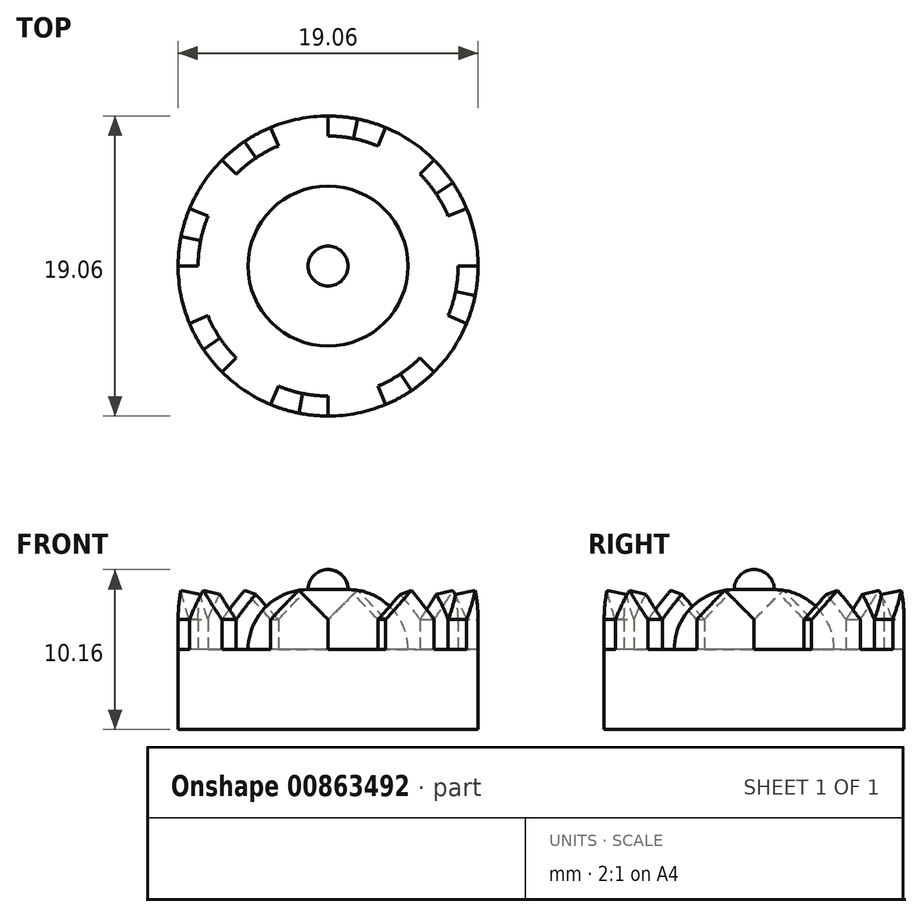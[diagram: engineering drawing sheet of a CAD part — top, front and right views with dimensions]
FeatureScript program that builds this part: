
annotation { "Feature Type Name" : "Feature", "Feature Type Description" : "" }
export const myFeature = defineFeature(function(context is Context, id is Id, definition is map)
    precondition{}
    {
        {
            var Q0;
            Q0=qCreatedBy(makeId("Top.planeOp"),FACE);
            var sketch = newSketch(context, id + "F0", { "sketchPlane" : qUnion([Q0])});
            skCircle(sketch, "E0", {"center": v(0, 0) * mm, "radius": 9.53 * mm});
            skLineSegment(sketch, "E1", {"start": v(0, 9.53) * mm, "end": v(0, 8.26) * mm});
            skLineSegment(sketch, "E2", {"start": v(3.16, 7.63) * mm, "end": v(3.65, 8.8) * mm});
            skLineSegment(sketch, "E3", {"start": v(5.84, 5.84) * mm, "end": v(6.74, 6.74) * mm});
            skLineSegment(sketch, "E4", {"start": v(8.26, 0) * mm, "end": v(9.77, 0) * mm});
            skLineSegment(sketch, "E5", {"start": v(7.63, 3.16) * mm, "end": v(8.8, 3.65) * mm});
            skArc(sketch, "E6", {"start": v(3.16, 7.63) * mm, "mid": v(1.61, 8.1) * mm, "end": v(0, 8.26) * mm});
            skArc(sketch, "E7.trimOffspring", {"start": v(7.63, 3.16) * mm, "mid": v(6.86, 4.59) * mm, "end": v(5.84, 5.84) * mm});
            skLineSegment(sketch, "E8", {"start": v(5.84, -5.84) * mm, "end": v(6.74, -6.74) * mm});
            skLineSegment(sketch, "E9", {"start": v(7.63, -3.16) * mm, "end": v(8.8, -3.65) * mm});
            skLineSegment(sketch, "E10", {"start": v(3.16, -7.63) * mm, "end": v(3.65, -8.8) * mm});
            skArc(sketch, "E11.trimOffspring", {"start": v(7.63, -3.16) * mm, "mid": v(8.1, -1.61) * mm, "end": v(8.26, 0) * mm});
            skArc(sketch, "E12.trimOffspring", {"start": v(3.16, -7.63) * mm, "mid": v(4.59, -6.86) * mm, "end": v(5.84, -5.84) * mm});
            skLineSegment(sketch, "E13", {"start": v(-8.26, 0) * mm, "end": v(-9.53, 0) * mm});
            skLineSegment(sketch, "E14", {"start": v(-5.84, 5.84) * mm, "end": v(-6.74, 6.74) * mm});
            skLineSegment(sketch, "E15", {"start": v(-7.63, 3.16) * mm, "end": v(-8.8, 3.65) * mm});
            skLineSegment(sketch, "E16", {"start": v(-3.16, 7.63) * mm, "end": v(-3.65, 8.8) * mm});
            skLineSegment(sketch, "E17", {"start": v(-7.63, -3.16) * mm, "end": v(-8.8, -3.65) * mm});
            skLineSegment(sketch, "E18", {"start": v(-5.84, -5.84) * mm, "end": v(-6.74, -6.74) * mm});
            skLineSegment(sketch, "E19", {"start": v(-3.16, -7.63) * mm, "end": v(-3.65, -8.8) * mm});
            skArc(sketch, "E20.trimOffspring", {"start": v(-3.16, -7.63) * mm, "mid": v(-1.61, -8.1) * mm, "end": v(0, -8.26) * mm});
            skArc(sketch, "E21.trimOffspring", {"start": v(-7.63, -3.16) * mm, "mid": v(-6.86, -4.59) * mm, "end": v(-5.84, -5.84) * mm});
            skArc(sketch, "E22.trimOffspring", {"start": v(-7.63, 3.16) * mm, "mid": v(-8.1, 1.61) * mm, "end": v(-8.26, 0) * mm});
            skArc(sketch, "E23.trimOffspring", {"start": v(-3.16, 7.63) * mm, "mid": v(-4.59, 6.86) * mm, "end": v(-5.84, 5.84) * mm});
            skLineSegment(sketch, "E24.trimOffspring", {"start": v(0, -8.26) * mm, "end": v(0, -9.53) * mm});
            skSolve(sketch);
        }
        {
            var Q0;
            {var subQ1=sQuery(id+"F0.wireOp",EDGE,"E1");var subQ3=sQuery(id+"F0.wireOp",EDGE,"E6");var subQ4=makeQuery(id+"F0.imprint","INTERSECT",VERTEX,{"disambiguationData":[OD(0.0)],"derivedFrom":[subQ1,subQ3]});Q0=makeQuery(id+"F0.imprint","IMPRINT",FACE,{"disambiguationData":[TD([[makeQuery(id+"F0.imprint","IMPRINT",EDGE,{"disambiguationData":[TD([[subQ4,1.0]])],"derivedFrom":subQ3}),1.0]])]});}
            var Q1;
            {var subQ0=sQuery(id+"F0.wireOp",EDGE,"E1");var subQ2=sQuery(id+"F0.wireOp",EDGE,"E6");var subQ3=makeQuery(id+"F0.imprint","INTERSECT",VERTEX,{"disambiguationData":[OD(0.0)],"derivedFrom":[subQ0,subQ2]});Q1=makeQuery(id+"F0.imprint","IMPRINT",FACE,{"disambiguationData":[TD([[makeQuery(id+"F0.imprint","IMPRINT",EDGE,{"disambiguationData":[TD([[subQ3,-1.0]])],"derivedFrom":subQ2}),1.0]])]});}
            var Q2;
            {var subQ1=sQuery(id+"F0.wireOp",EDGE,"E1");var subQ3=sQuery(id+"F0.wireOp",EDGE,"E6");var subQ4=makeQuery(id+"F0.imprint","INTERSECT",VERTEX,{"disambiguationData":[OD(1.0)],"derivedFrom":[subQ1,subQ3]});Q2=makeQuery(id+"F0.imprint","IMPRINT",FACE,{"disambiguationData":[TD([[makeQuery(id+"F0.imprint","IMPRINT",EDGE,{"disambiguationData":[TD([[subQ4,-1.0]])],"derivedFrom":subQ3}),1.0]])]});}
            var Q3;
            {var subQ1=sQuery(id+"F0.wireOp",EDGE,"E4");var subQ3=sQuery(id+"F0.wireOp",EDGE,"E6");var subQ4=makeQuery(id+"F0.imprint","INTERSECT",VERTEX,{"derivedFrom":[subQ1,subQ3]});Q3=makeQuery(id+"F0.imprint","IMPRINT",FACE,{"disambiguationData":[TD([[makeQuery(id+"F0.imprint","IMPRINT",EDGE,{"disambiguationData":[TD([[subQ4,-1.0]])],"derivedFrom":subQ3}),1.0]])]});}
            var Q4;
            {var subQ1=sQuery(id+"F0.wireOp",EDGE,"E3");var subQ3=sQuery(id+"F0.wireOp",EDGE,"E6");var subQ4=makeQuery(id+"F0.imprint","INTERSECT",VERTEX,{"derivedFrom":[subQ1,subQ3]});Q4=makeQuery(id+"F0.imprint","IMPRINT",FACE,{"disambiguationData":[TD([[makeQuery(id+"F0.imprint","IMPRINT",EDGE,{"disambiguationData":[TD([[subQ4,1.0]])],"derivedFrom":subQ3}),1.0]])]});}
            var Q5;
            {var subQ1=sQuery(id+"F0.wireOp",EDGE,"E2");var subQ3=sQuery(id+"F0.wireOp",EDGE,"E6");var subQ4=makeQuery(id+"F0.imprint","INTERSECT",VERTEX,{"derivedFrom":[subQ1,subQ3]});Q5=makeQuery(id+"F0.imprint","IMPRINT",FACE,{"disambiguationData":[TD([[makeQuery(id+"F0.imprint","IMPRINT",EDGE,{"disambiguationData":[TD([[subQ4,1.0]])],"derivedFrom":subQ3}),1.0]])]});}
            var Q6;
            {var subQ0=sQuery(id+"F0.wireOp",EDGE,"E2");var subQ1=sQuery(id+"F0.wireOp",EDGE,"E0");var subQ2=makeQuery(id+"F0.imprint","INTERSECT",VERTEX,{"derivedFrom":[subQ1,subQ0]});Q6=makeQuery(id+"F0.imprint","IMPRINT",FACE,{"disambiguationData":[TD([[makeQuery(id+"F0.imprint","IMPRINT",EDGE,{"disambiguationData":[TD([[subQ2,1.0]])],"derivedFrom":subQ1}),1.0]])]});}
            var Q7;
            {var subQ0=sQuery(id+"F0.wireOp",EDGE,"E5");var subQ1=sQuery(id+"F0.wireOp",EDGE,"E0");var subQ2=makeQuery(id+"F0.imprint","INTERSECT",VERTEX,{"derivedFrom":[subQ1,subQ0]});Q7=makeQuery(id+"F0.imprint","IMPRINT",FACE,{"disambiguationData":[TD([[makeQuery(id+"F0.imprint","IMPRINT",EDGE,{"disambiguationData":[TD([[subQ2,1.0]])],"derivedFrom":subQ1}),1.0]])]});}
            var Q8;
            {var subQ8=sQuery(id+"F0.wireOp",EDGE,"E8");Q8=makeQuery(id+"F0.imprint","IMPRINT",FACE,{"disambiguationData":[TD([[makeQuery(id+"F0.imprint","IMPRINT",EDGE,{"derivedFrom":subQ8}),1.0]])]});}
            extrude(context, id + "F1", {"entities" : qUnion([Q0, Q1, Q2, Q3, Q4, Q5, Q6, Q7, Q8]), "depth" : 5.08 * mm, "offsetDistance" : 25.4 * mm});
        }
        {
            var Q0;
            {var subQ0=sQuery(id+"F0.wireOp",EDGE,"E1");var subQ1=sQuery(id+"F0.wireOp",EDGE,"E0");var subQ2=makeQuery(id+"F0.imprint","INTERSECT",VERTEX,{"disambiguationData":[OD(0.0)],"derivedFrom":[subQ1,subQ0]});Q0=makeQuery(id+"F0.imprint","IMPRINT",FACE,{"disambiguationData":[TD([[makeQuery(id+"F0.imprint","IMPRINT",EDGE,{"disambiguationData":[TD([[subQ2,1.0]])],"derivedFrom":subQ1}),1.0]])]});}
            var Q1;
            {var subQ0=sQuery(id+"F0.wireOp",EDGE,"E3");var subQ1=sQuery(id+"F0.wireOp",EDGE,"E0");var subQ2=makeQuery(id+"F0.imprint","INTERSECT",VERTEX,{"derivedFrom":[subQ1,subQ0]});Q1=makeQuery(id+"F0.imprint","IMPRINT",FACE,{"disambiguationData":[TD([[makeQuery(id+"F0.imprint","IMPRINT",EDGE,{"disambiguationData":[TD([[subQ2,1.0]])],"derivedFrom":subQ1}),1.0]])]});}
            var Q2;
            {var subQ0=sQuery(id+"F0.wireOp",EDGE,"E8");Q2=makeQuery(id+"F0.imprint","IMPRINT",FACE,{"disambiguationData":[TD([[makeQuery(id+"F0.imprint","IMPRINT",EDGE,{"derivedFrom":subQ0}),-1.0]])]});}
            var Q3;
            {var subQ0=sQuery(id+"F0.wireOp",EDGE,"E9");Q3=makeQuery(id+"F0.imprint","IMPRINT",FACE,{"disambiguationData":[TD([[makeQuery(id+"F0.imprint","IMPRINT",EDGE,{"derivedFrom":subQ0}),1.0]])]});}
            var Q4;
            {var subQ0=sQuery(id+"F0.wireOp",EDGE,"E19");Q4=makeQuery(id+"F0.imprint","IMPRINT",FACE,{"disambiguationData":[TD([[makeQuery(id+"F0.imprint","IMPRINT",EDGE,{"derivedFrom":subQ0}),1.0]])]});}
            var Q5;
            {var subQ0=sQuery(id+"F0.wireOp",EDGE,"E17");Q5=makeQuery(id+"F0.imprint","IMPRINT",FACE,{"disambiguationData":[TD([[makeQuery(id+"F0.imprint","IMPRINT",EDGE,{"derivedFrom":subQ0}),1.0]])]});}
            var Q6;
            {var subQ0=sQuery(id+"F0.wireOp",EDGE,"E13");Q6=makeQuery(id+"F0.imprint","IMPRINT",FACE,{"disambiguationData":[TD([[makeQuery(id+"F0.imprint","IMPRINT",EDGE,{"derivedFrom":subQ0}),-1.0]])]});}
            var Q7;
            {var subQ0=sQuery(id+"F0.wireOp",EDGE,"E14");Q7=makeQuery(id+"F0.imprint","IMPRINT",FACE,{"disambiguationData":[TD([[makeQuery(id+"F0.imprint","IMPRINT",EDGE,{"derivedFrom":subQ0}),-1.0]])]});}
            extrude(context, id + "F2", {"entities" : qUnion([Q0, Q1, Q2, Q3, Q4, Q5, Q6, Q7]), "operationType" : NewBodyOperationType.ADD, "depth" : 8.9 * mm, "offsetDistance" : 25.4 * mm});
        }
        {
            var Q0;
            Q0=makeQuery(id+"F2.opExtrude","CAP_EDGE",EDGE,{"disambiguationData":[OSD([sQuery(id+"F0.wireOp",EDGE,"E2")])],"isStart":false});
            var Q1;
            Q1=makeQuery(id+"F2.opExtrude","CAP_EDGE",EDGE,{"disambiguationData":[OSD([sQuery(id+"F0.wireOp",EDGE,"E1")])],"isStart":false});
            var Q2;
            Q2=makeQuery(id+"F2.opExtrude","CAP_EDGE",EDGE,{"disambiguationData":[OSD([sQuery(id+"F0.wireOp",EDGE,"E5")])],"isStart":false});
            var Q3;
            Q3=makeQuery(id+"F2.opExtrude","CAP_EDGE",EDGE,{"disambiguationData":[OSD([sQuery(id+"F0.wireOp",EDGE,"E3")])],"isStart":false});
            var Q4;
            Q4=makeQuery(id+"F2.opExtrude","CAP_EDGE",EDGE,{"disambiguationData":[OSD([sQuery(id+"F0.wireOp",EDGE,"E10")])],"isStart":false});
            var Q5;
            Q5=makeQuery(id+"F2.opExtrude","CAP_EDGE",EDGE,{"disambiguationData":[OSD([sQuery(id+"F0.wireOp",EDGE,"E8")])],"isStart":false});
            var Q6;
            Q6=makeQuery(id+"F2.opExtrude","CAP_EDGE",EDGE,{"disambiguationData":[OSD([sQuery(id+"F0.wireOp",EDGE,"E9")])],"isStart":false});
            var Q7;
            Q7=makeQuery(id+"F2.opExtrude","CAP_EDGE",EDGE,{"disambiguationData":[OSD([sQuery(id+"F0.wireOp",EDGE,"E4")])],"isStart":false});
            var Q8;
            Q8=makeQuery(id+"F2.opExtrude","CAP_EDGE",EDGE,{"disambiguationData":[OSD([sQuery(id+"F0.wireOp",EDGE,"E24.trimOffspring")])],"isStart":false});
            var Q9;
            Q9=makeQuery(id+"F2.opExtrude","CAP_EDGE",EDGE,{"disambiguationData":[OSD([sQuery(id+"F0.wireOp",EDGE,"E19")])],"isStart":false});
            var Q10;
            Q10=makeQuery(id+"F2.opExtrude","CAP_EDGE",EDGE,{"disambiguationData":[OSD([sQuery(id+"F0.wireOp",EDGE,"E18")])],"isStart":false});
            var Q11;
            Q11=makeQuery(id+"F2.opExtrude","CAP_EDGE",EDGE,{"disambiguationData":[OSD([sQuery(id+"F0.wireOp",EDGE,"E17")])],"isStart":false});
            var Q12;
            Q12=makeQuery(id+"F2.opExtrude","CAP_EDGE",EDGE,{"disambiguationData":[OSD([sQuery(id+"F0.wireOp",EDGE,"E13")])],"isStart":false});
            var Q13;
            Q13=makeQuery(id+"F2.opExtrude","CAP_EDGE",EDGE,{"disambiguationData":[OSD([sQuery(id+"F0.wireOp",EDGE,"E15")])],"isStart":false});
            var Q14;
            Q14=makeQuery(id+"F2.opExtrude","CAP_EDGE",EDGE,{"disambiguationData":[OSD([sQuery(id+"F0.wireOp",EDGE,"E14")])],"isStart":false});
            var Q15;
            Q15=makeQuery(id+"F2.opExtrude","CAP_EDGE",EDGE,{"disambiguationData":[OSD([sQuery(id+"F0.wireOp",EDGE,"E16")])],"isStart":false});
            chamfer(context, id + "F3", {"entities" : qUnion([Q0, Q1, Q2, Q3, Q4, Q5, Q6, Q7, Q8, Q9, Q10, Q11, Q12, Q13, Q14, Q15]), "width" : 1.9 * mm, "tangentPropagation" : true});
        }
        {
            var Q0;
            Q0=makeQuery(id+"F1.opExtrude","CAP_FACE",FACE,{"disambiguationData":[OSD([sQuery(id+"F0.wireOp",EDGE,"E0"),sQuery(id+"F0.wireOp",EDGE,"E1"),sQuery(id+"F0.wireOp",EDGE,"E2"),sQuery(id+"F0.wireOp",EDGE,"E3"),sQuery(id+"F0.wireOp",EDGE,"E4"),sQuery(id+"F0.wireOp",EDGE,"E5"),sQuery(id+"F0.wireOp",EDGE,"E6"),sQuery(id+"F0.wireOp",EDGE,"E7.trimOffspring"),sQuery(id+"F0.wireOp",EDGE,"E8"),sQuery(id+"F0.wireOp",EDGE,"E9"),sQuery(id+"F0.wireOp",EDGE,"E10"),sQuery(id+"F0.wireOp",EDGE,"E11.trimOffspring"),sQuery(id+"F0.wireOp",EDGE,"E12.trimOffspring"),sQuery(id+"F0.wireOp",EDGE,"E13"),sQuery(id+"F0.wireOp",EDGE,"E14"),sQuery(id+"F0.wireOp",EDGE,"E15"),sQuery(id+"F0.wireOp",EDGE,"E16"),sQuery(id+"F0.wireOp",EDGE,"E17"),sQuery(id+"F0.wireOp",EDGE,"E18"),sQuery(id+"F0.wireOp",EDGE,"E19"),sQuery(id+"F0.wireOp",EDGE,"E20.trimOffspring"),sQuery(id+"F0.wireOp",EDGE,"E21.trimOffspring"),sQuery(id+"F0.wireOp",EDGE,"E22.trimOffspring"),sQuery(id+"F0.wireOp",EDGE,"E23.trimOffspring"),sQuery(id+"F0.wireOp",EDGE,"E24.trimOffspring")])],"isStart":false});
            var sketch = newSketch(context, id + "F4", { "sketchPlane" : qUnion([Q0])});
            skCircle(sketch, "E25", {"center": v(0, 0) * mm, "radius": 5.08 * mm});
            skSolve(sketch);
        }
        {
            var Q0;
            Q0=makeQuery(id+"F4.imprint","IMPRINT",FACE,{"disambiguationData":[TD([[makeQuery(id+"F4.imprint","IMPRINT",EDGE,{"derivedFrom":sQuery(id+"F4.wireOp",EDGE,"E25")}),1.0]])]});
            extrude(context, id + "F5", {"entities" : qUnion([Q0]), "operationType" : NewBodyOperationType.ADD, "depth" : 3.8 * mm, "offsetDistance" : 25.4 * mm});
        }
        {
            var Q0;
            Q0=makeQuery(id+"F5.opExtrude","CAP_EDGE",EDGE,{"disambiguationData":[OSD([sQuery(id+"F4.wireOp",EDGE,"E25")])],"isStart":false});
            fillet(context, id + "F6", {"entities" : qUnion([Q0]), "radius" : 3.8 * mm, "tangentPropagation" : true, "allowEdgeOverflow" : false});
        }
        {
            var Q0;
            Q0=makeQuery(id+"F5.opExtrude","CAP_FACE",FACE,{"disambiguationData":[OSD([sQuery(id+"F4.wireOp",EDGE,"E25")])],"isStart":false});
            var sketch = newSketch(context, id + "F7", { "sketchPlane" : qUnion([Q0])});
            skCircle(sketch, "E26", {"center": v(0, 0) * mm, "radius": 1.27 * mm});
            skSolve(sketch);
        }
        {
            var Q0;
            Q0=makeQuery(id+"F7.imprint","IMPRINT",FACE,{"disambiguationData":[TD([[makeQuery(id+"F7.imprint","IMPRINT",EDGE,{"derivedFrom":sQuery(id+"F7.wireOp",EDGE,"E26")}),1.0]])]});
            extrude(context, id + "F8", {"entities" : qUnion([Q0]), "operationType" : NewBodyOperationType.ADD, "depth" : 1.27 * mm, "offsetDistance" : 25.4 * mm});
        }
        {
            var Q0;
            Q0=makeQuery(id+"F8.opExtrude","CAP_EDGE",EDGE,{"disambiguationData":[OSD([sQuery(id+"F7.wireOp",EDGE,"E26")])],"isStart":false});
            fillet(context, id + "F9", {"entities" : qUnion([Q0]), "radius" : 1.27 * mm, "tangentPropagation" : true, "allowEdgeOverflow" : false});
        }
    });
